# Revit family: Gira_282026
name_source: partatom
category: Electrical Fixtures
revit_build: Autodesk Revit 2017 (Build: 20160225_1515(x64)
units: mm (PartAtom-declared; Revit-internal decimal feet)

## family parameters
Cut with Voids When Loaded = No
Host = Face
Maintain Annotation Orientation = Yes
Part Type = Normal
Room Calculation Point = No
Round Connector Dimension = Use Diameter
Shared = No

## types (1)
- Razor sock. 115 - 230 V System 55 c.alum.
    Assembly arrangement = Basic element with adapter plate
    Available = No
    BIM (1) = https://media.stage.bim.site
    Category = Razor socket outlet
    Colour = Aluminium
    Data sheet (1) = https://katalog.gira.de
    Default Elevation = 1219 mm
    Description = Razor sock.115-230V Sys55 CAl,Razor socket outlet (DIN EN 61558 2-5) 115 - 230 V~ for cover frame, 2-gang without crossbar,System 55,colour aluminium,
    GTIN = 4010337016793
    HAN = 282026
    Halogen free = No
    HeinzeBIM = https://bimportal.heinze.de
    Manufacturer = Gira
    Manufacturer URL = https://www.gira.de
    Material = Other
    Material quality = Other
    Mounting method = Flush mounted (plaster)
    Name = Razor sock. 115 - 230 V System 55 c.alum.
    Nominal voltage high value = 230
    Nominal voltage low value = 115
    Surface protection = Other
    Transparent = No
    URL = http://katalog.gira.de
    Voltage reversible = Yes
    With hinged lid = No

## geometry (parser evidence)
native form markers: Sweep x3
no freeform markers — native parametric forms only
